# Revit family: Faucet-Deck_Mount-Bath-KOHLER-SINGULIER-K-10873T_1
name_source: partatom
category: Plumbing Fixtures
revit_build: Autodesk Revit 2017 (Build: 20160225_1515(x64)
units: mm (PartAtom-declared; Revit-internal decimal feet)

## family parameters
Cut with Voids When Loaded = No
Host = Face
OmniClass Number = 23.31.11.00
OmniClass Title = Faucets
Part Type = Normal
Room Calculation Point = No
Round Connector Dimension = Use Diameter
Shared = No

## types (6) — shared parameters
ADA Compliant = No
Assembly Code = D2010
CW Connection = Yes
Cold Water Inlet = Cold Water Inlet
Date Modified = 07/01/2020
Default Elevation = 36"
Drain Included = No
HW Connection = Yes
Handle Clearance = 3 3/8"
Handle Height = 2 3/4"
Height = 9 1/8"
Hot Water Inlet = Hot Water Inlet
Length = 5 5/16"
Manufacturer = KOHLER Co.
Master Format 2014 = 22 41 39
Master Format 2014 Name = Residential Faucets, Supplies, and Trim
Material = Solid Brass Construction
Pressure = 45.00 psi
Product Name = SINGULIER
Spout Reach = 5 5/16"
URL = http://www.kohler.com.cn
Vent Connection = No
Waste Connection = No
Waste Water Outlet = Waste Water Outlet
WaterSense Certified = No

## per-type parameters (varying)
| type | 4 | B4 | Description | Finish | Flow Rate | Handshower Height | Model | Product Documentation Link | Product Page URL | Type |
| CP-Polished Chrome | Yes | No |  | Kohler-Metal-CP-Polished_Chrome | 4 GPM | 9 7/16" | K-10873T-4-CP |  |  | 1 |
| BN-Roman Silver | Yes | No |  | Kohler-Metal-BN-Roman_Silver | 4 GPM | 9 7/16" | K-10873T-4-BN |  |  | 2 |
| AF-Flange Gold | Yes | No |  | Kohler-Metal-AF-Flange_Gold | 4 GPM | 9 7/16" | K-10873T-4-AF |  |  | 3 |
| B4, CP-Polished Chrome | No | Yes | Xinjiali three hole cylinder side faucet | Kohler-Metal-CP-Polished_Chrome | 10 GPM | 10 5/16" | K-10873T-B4-CP | https://files.kohler.com.cn | https://www.kohler.com.cn | 4 |
| B4, BN-Roman Silver | No | Yes | Xinjiali three hole cylinder side faucet | Kohler-Metal-BN-Roman_Silver | 10 GPM | 10 5/16" | K-10873T-B4-BN | https://files.kohler.com.cn | https://www.kohler.com.cn | 5 |
| B4, AF-Flange Gold | No | Yes | Xinjiali three hole cylinder side faucet | Kohler-Metal-AF-Flange_Gold | 10 GPM | 10 5/16" | K-10873T-B4-AF | https://files.kohler.com.cn | https://www.kohler.com.cn | 6 |

## geometry (parser evidence)
native form markers: Sweep x8
no freeform markers — native parametric forms only
